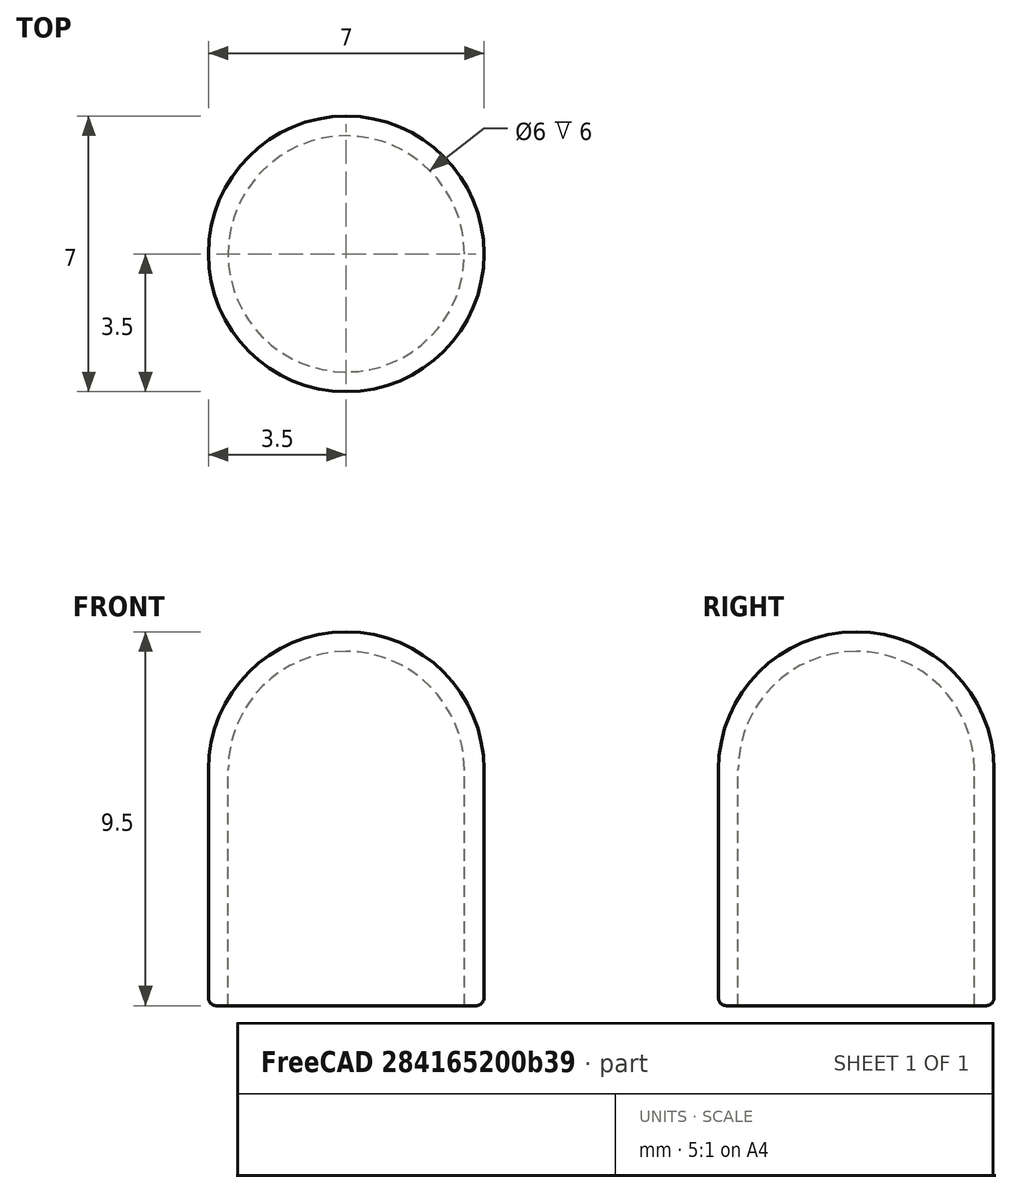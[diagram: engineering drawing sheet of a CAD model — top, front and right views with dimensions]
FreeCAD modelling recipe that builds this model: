
FCSTD DOCUMENT  (FreeCAD 0.17R13541 (Git))
Label: Toggle Switch Cap
License: All rights reserved
LicenseURL: http://en.wikipedia.org/wiki/All_rights_reserved
objects: Part::Cylinder×2, Part::Cut×2, Part::Sphere×2, Part::Fillet×1, Part::Fuse×1
note: 8 computed .brp shape members not serialized (recipe doc carries the construction recipe); baked Part::Feature solids carry a one-line shape summary decoded from their .brp

FEATURE [Part::Cylinder] Cylinder  label="Cilindro exterior"
  Angle = 360
  AttacherType = Attacher::AttachEngine3D
  Height = 6
  Radius = 3.5
FEATURE [Part::Cylinder] Cylinder001  label="Cilindro interior"
  Angle = 360
  AttacherType = Attacher::AttachEngine3D
  Height = 6
  Radius = 3
FEATURE [Part::Cut] Cut  label="Cilindro"
  Base = -> Cylinder
  Refine = true
  Tool = -> Cylinder001
FEATURE [Part::Fillet] Fillet  label="Cilindro canteado"
  Base = -> Cut
  Edges = 1 edges r=0.2: [Edge3]
FEATURE [Part::Sphere] Sphere  label="Esfera exterior"
  Angle1 = -90
  Angle2 = 0
  Angle3 = 360
  AttacherType = Attacher::AttachEngine3D
  Placement = pos=(0,0,7) rot=(1,0,0;3.14159rad)
  Radius = 3.5
FEATURE [Part::Sphere] Sphere001  label="Esfera interior"
  Angle1 = -90
  Angle2 = 0
  Angle3 = 360
  AttacherType = Attacher::AttachEngine3D
  Placement = pos=(0,0,7) rot=(1,0,0;3.14159rad)
  Radius = 3
FEATURE [Part::Cut] Cut001  label="Esfera"
  Base = -> Sphere
  Placement = pos=(0,0,-1) rot=(0,0,1;0rad)
  Refine = true
  Tool = -> Sphere001
FEATURE [Part::Fuse] Fusion  label="Toggle Switch Cap"
  Base = -> Fillet
  Refine = true
  Tool = -> Cut001
